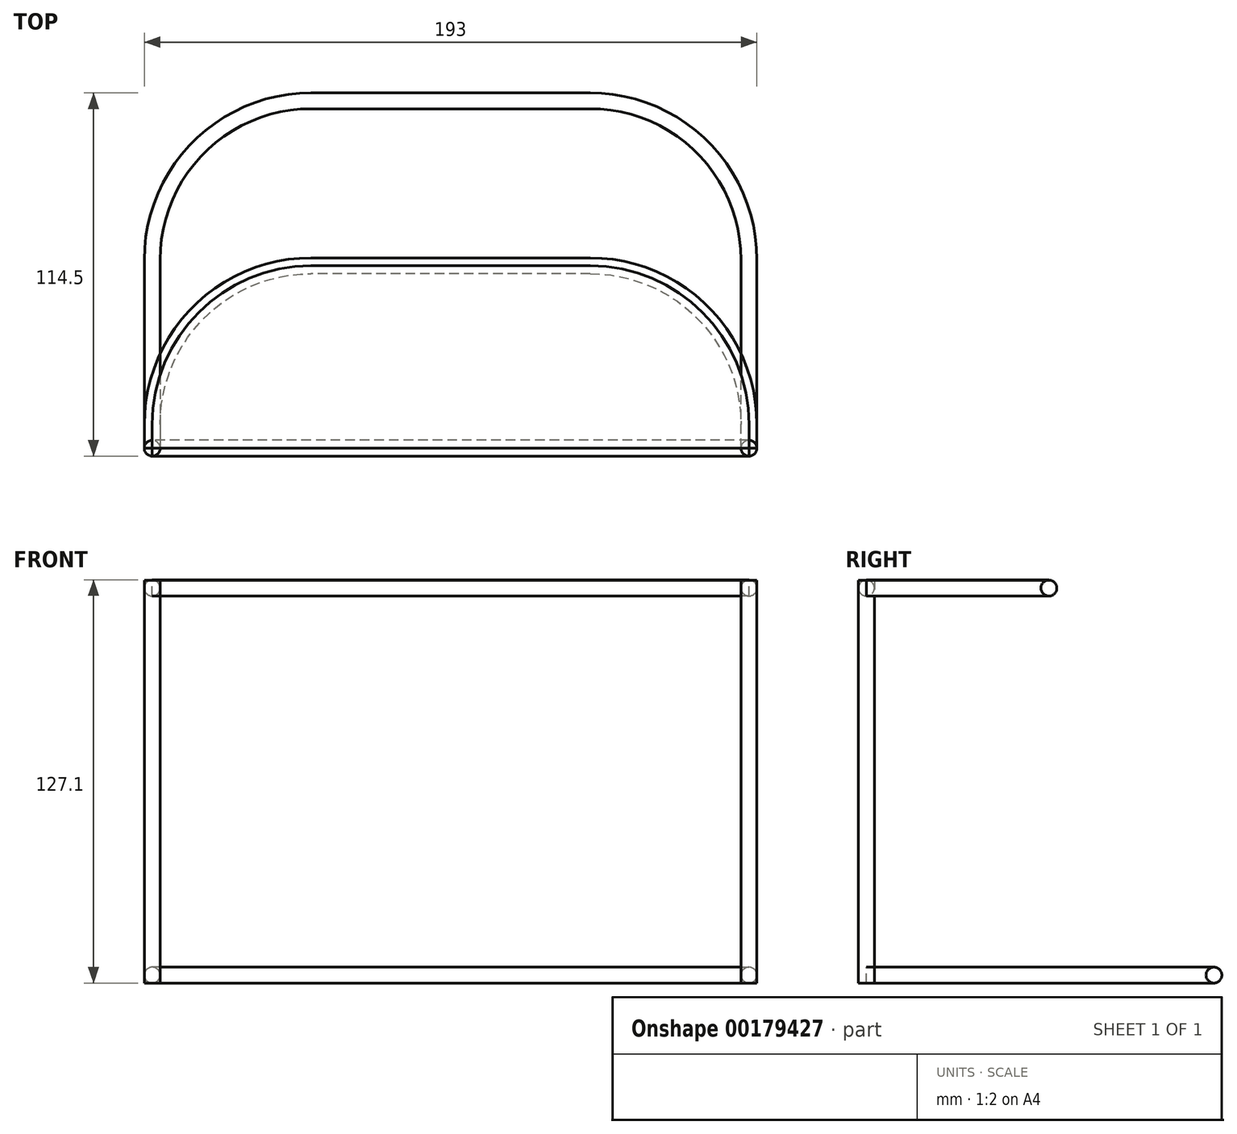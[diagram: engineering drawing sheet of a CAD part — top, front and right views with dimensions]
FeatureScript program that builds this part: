
annotation { "Feature Type Name" : "Feature", "Feature Type Description" : "" }
export const myFeature = defineFeature(function(context is Context, id is Id, definition is map)
    precondition{}
    {
        {
            var Q0;
            Q0=qCreatedBy(makeId("Top.planeOp"),FACE);
            var sketch = newSketch(context, id + "F0", { "sketchPlane" : qUnion([Q0])});
            skLineSegment(sketch, "E0", {"start": v(-94, 0) * mm, "end": v(94, 0) * mm, "construction": true});
            skCircle(sketch, "E1", {"center": v(-94, 0) * mm, "radius": 2.5 * mm});
            skCircle(sketch, "E2", {"center": v(94, 0) * mm, "radius": 2.5 * mm});
            skSolve(sketch);
        }
        {
            var Q0;
            Q0=makeQuery(id+"F0.imprint","IMPRINT",FACE,{"disambiguationData":[TD([[makeQuery(id+"F0.imprint","IMPRINT",EDGE,{"derivedFrom":sQuery(id+"F0.wireOp",EDGE,"E2")}),1.0]])]});
            var Q1;
            Q1=makeQuery(id+"F0.imprint","IMPRINT",FACE,{"disambiguationData":[TD([[makeQuery(id+"F0.imprint","IMPRINT",EDGE,{"derivedFrom":sQuery(id+"F0.wireOp",EDGE,"E1")}),1.0]])]});
            extrude(context, id + "F1", {"entities" : qUnion([Q0, Q1]), "depth" : 127 * mm});
        }
        {
            var Q0;
            Q0=qCreatedBy(makeId("Top.planeOp"),FACE);
            cPlane(context, id + "F2", {"entities" : qUnion([Q0]), "cplaneType" : CPlaneType.OFFSET, "offset" : 124.5 * mm, "width" : 150 * mm, "height" : 150 * mm});
        }
        {
            var Q0;
            Q0=qCreatedBy(id+"F2.planeOp",FACE);
            var sketch = newSketch(context, id + "F3", { "sketchPlane" : qUnion([Q0])});
            skCircle(sketch, "E3.0", {"center": v(-94, 0) * mm, "radius": 2.5 * mm});
            skCircle(sketch, "E4.0", {"center": v(94, 0) * mm, "radius": 2.5 * mm});
            skLineSegment(sketch, "E5", {"start": v(-94, 0) * mm, "end": v(94, 0) * mm});
            skSolve(sketch);
        }
        {
            var Q0;
            Q0=qCreatedBy(makeId("Right.planeOp"),FACE);
            cPlane(context, id + "F4", {"entities" : qUnion([Q0]), "cplaneType" : CPlaneType.OFFSET, "offset" : (188 / 2) * mm, "width" : 150 * mm, "height" : 150 * mm});
        }
        {
            var Q0;
            Q0=qCreatedBy(id+"F4.planeOp",FACE);
            var sketch = newSketch(context, id + "F5", { "sketchPlane" : qUnion([Q0])});
            skPoint(sketch, "E6.0", {"position": v(0, 124.5) * mm});
            skCircle(sketch, "E7", {"center": v(0, 124.5) * mm, "radius": 2.5 * mm});
            skSolve(sketch);
        }
        {
            var Q0;
            Q0=makeQuery(id+"F5.imprint","IMPRINT",FACE,{"disambiguationData":[TD([[makeQuery(id+"F5.imprint","IMPRINT",EDGE,{"derivedFrom":sQuery(id+"F5.wireOp",EDGE,"E7")}),1.0]])]});
            var Q1;
            Q1=sQuery(id+"F5.wireOp",EDGE,"E7");
            var Q2;
            Q2=sQuery(id+"F3.wireOp",EDGE,"E5");
            var Q3;
            Q3=sQuery(id+"F3.wireOp",EDGE,"E5");
            sweep(context, id + "F6", {"profiles" : qUnion([Q0]), "surfaceProfiles" : qUnion([Q1, Q2]), "path" : qUnion([Q3])});
        }
        {
            var Q0;
            Q0=qCreatedBy(makeId("Front.planeOp"),FACE);
            var sketch = newSketch(context, id + "F7", { "sketchPlane" : qUnion([Q0])});
            skCircle(sketch, "E8", {"center": v(94, 2.5) * mm, "radius": 2.5 * mm});
            skSolve(sketch);
        }
        {
            var Q0;
            Q0=qCreatedBy(makeId("Top.planeOp"),FACE);
            var sketch = newSketch(context, id + "F8", { "sketchPlane" : qUnion([Q0])});
            skLineSegment(sketch, "E9", {"start": v(94, 0) * mm, "end": v(94, 59.5) * mm});
            skLineSegment(sketch, "E10", {"start": v(44, 109.5) * mm, "end": v(-44, 109.5) * mm});
            skLineSegment(sketch, "E11", {"start": v(-94, 59.5) * mm, "end": v(-94, 0) * mm});
            skPoint(sketch, "E12.visualSharp", {"position": v(-94, 109.5) * mm});
            skArc(sketch, "E12.filletArc", {"start": v(-44, 109.5) * mm, "mid": v(-79.36, 94.86) * mm, "end": v(-94, 59.5) * mm});
            skPoint(sketch, "E13.visualSharp", {"position": v(94, 109.5) * mm});
            skArc(sketch, "E13.filletArc", {"start": v(94, 59.5) * mm, "mid": v(79.36, 94.86) * mm, "end": v(44, 109.5) * mm});
            skSolve(sketch);
        }
        {
            var Q0;
            Q0=makeQuery(id+"F7.imprint","IMPRINT",FACE,{"disambiguationData":[TD([[makeQuery(id+"F7.imprint","IMPRINT",EDGE,{"derivedFrom":sQuery(id+"F7.wireOp",EDGE,"E8")}),1.0]])]});
            var Q1;
            Q1=sQuery(id+"F8.wireOp",EDGE,"E9");
            var Q2;
            Q2=sQuery(id+"F8.wireOp",EDGE,"E13.filletArc");
            var Q3;
            Q3=sQuery(id+"F8.wireOp",EDGE,"E10");
            var Q4;
            Q4=sQuery(id+"F8.wireOp",EDGE,"E12.filletArc");
            var Q5;
            Q5=sQuery(id+"F8.wireOp",EDGE,"E11");
            sweep(context, id + "F9", {"profiles" : qUnion([Q0]), "path" : qUnion([Q1, Q2, Q3, Q4, Q5])});
        }
        {
            var Q0;
            Q0=qCreatedBy(id+"F2.planeOp",FACE);
            var sketch = newSketch(context, id + "F10", { "sketchPlane" : qUnion([Q0])});
            skLineSegment(sketch, "E14", {"start": v(94, 0) * mm, "end": v(94, 7.5) * mm});
            skLineSegment(sketch, "E15", {"start": v(44, 57.5) * mm, "end": v(-44, 57.5) * mm});
            skLineSegment(sketch, "E16", {"start": v(-94, 7.5) * mm, "end": v(-94, 0) * mm});
            skPoint(sketch, "E17.visualSharp", {"position": v(-94, 57.5) * mm});
            skArc(sketch, "E17.filletArc", {"start": v(-44, 57.5) * mm, "mid": v(-79.36, 42.86) * mm, "end": v(-94, 7.5) * mm});
            skPoint(sketch, "E18.visualSharp", {"position": v(94, 57.5) * mm});
            skArc(sketch, "E18.filletArc", {"start": v(94, 7.5) * mm, "mid": v(79.36, 42.86) * mm, "end": v(44, 57.5) * mm});
            skSolve(sketch);
        }
        {
            var Q0;
            Q0=qCreatedBy(makeId("Front.planeOp"),FACE);
            var sketch = newSketch(context, id + "F11", { "sketchPlane" : qUnion([Q0])});
            skPoint(sketch, "E19.0", {"position": v(94, 124.5) * mm});
            skCircle(sketch, "E20", {"center": v(94, 124.5) * mm, "radius": 2.5 * mm});
            skSolve(sketch);
        }
        {
            var Q0;
            Q0=makeQuery(id+"F11.imprint","IMPRINT",FACE,{"disambiguationData":[TD([[makeQuery(id+"F11.imprint","IMPRINT",EDGE,{"derivedFrom":sQuery(id+"F11.wireOp",EDGE,"E20")}),1.0]])]});
            var Q1;
            Q1=sQuery(id+"F10.wireOp",EDGE,"E14");
            var Q2;
            Q2=sQuery(id+"F10.wireOp",EDGE,"E18.filletArc");
            var Q3;
            Q3=sQuery(id+"F10.wireOp",EDGE,"E15");
            var Q4;
            Q4=sQuery(id+"F10.wireOp",EDGE,"E17.filletArc");
            var Q5;
            Q5=sQuery(id+"F10.wireOp",EDGE,"E16");
            sweep(context, id + "F12", {"profiles" : qUnion([Q0]), "path" : qUnion([Q1, Q2, Q3, Q4, Q5])});
        }
        {
            var Q0;
            Q0=qCreatedBy(id+"F2.planeOp",FACE);
            var sketch = newSketch(context, id + "F13", { "sketchPlane" : qUnion([Q0])});
            skArc(sketch, "E21", {"start": v(-44, 60) * mm, "mid": v(-81.12, 44.62) * mm, "end": v(-96.5, 7.5) * mm});
            skLineSegment(sketch, "E22", {"start": v(-96.5, 0) * mm, "end": v(-96.5, 7.5) * mm});
            skLineSegment(sketch, "E23", {"start": v(-44, 60) * mm, "end": v(44, 60) * mm});
            skArc(sketch, "E24", {"start": v(96.5, 7.5) * mm, "mid": v(81.12, 44.62) * mm, "end": v(44, 60) * mm});
            skLineSegment(sketch, "E25", {"start": v(96.5, 7.5) * mm, "end": v(96.5, 0) * mm});
            skSolve(sketch);
        }
        {
            var Q0;
            Q0=qCreatedBy(makeId("Top.planeOp"),FACE);
            cPlane(context, id + "F14", {"entities" : qUnion([Q0]), "cplaneType" : CPlaneType.OFFSET, "offset" : 2.5 * mm, "width" : 150 * mm, "height" : 150 * mm});
        }
        {
            var Q0;
            Q0=qCreatedBy(id+"F14.planeOp",FACE);
            var sketch = newSketch(context, id + "F15", { "sketchPlane" : qUnion([Q0])});
            skArc(sketch, "E26", {"start": v(-44, 112) * mm, "mid": v(-81.12, 96.62) * mm, "end": v(-96.5, 59.5) * mm});
            skLineSegment(sketch, "E27", {"start": v(-44, 112) * mm, "end": v(44, 112) * mm});
            skArc(sketch, "E28", {"start": v(96.5, 59.5) * mm, "mid": v(81.12, 96.62) * mm, "end": v(44, 112) * mm});
            skLineSegment(sketch, "E29", {"start": v(96.5, 59.5) * mm, "end": v(96.5, 0) * mm});
            skLineSegment(sketch, "E30", {"start": v(-96.5, 0) * mm, "end": v(-96.5, 59.5) * mm});
            skSolve(sketch);
        }
        {
            var Q0;
            Q0=qCreatedBy(makeId("Right.planeOp"),FACE);
            var sketch = newSketch(context, id + "F16", { "sketchPlane" : qUnion([Q0])});
            skPoint(sketch, "E31.0", {"position": v(60, 124.5) * mm});
            skPoint(sketch, "E32.0", {"position": v(112, 2.5) * mm});
            skFitSpline(sketch, "E33", {"points": [v(60, 124.5) * mm, v(112, 2.5) * mm], "startDerivative": vector(40.52, -242.4) * mm, "endDerivative": vector(1.83, -10.83) * mm});
            skSolve(sketch);
        }
        {
            var Q0;
            Q0 = qSketchRegion(id + "F13", true);
            var Q1;
            Q1 = qSketchRegion(id + "F15", true);
            var Q2;
            Q2 = qConstructionFilter(qBodyType(qCreatedBy(id + "F13" ,EDGE), BodyType.WIRE), ConstructionObject.NO);
            var Q3;
            Q3 = qConstructionFilter(qBodyType(qCreatedBy(id + "F15" ,EDGE), BodyType.WIRE), ConstructionObject.NO);
            var Q4;
            Q4 = qConstructionFilter(qBodyType(qCreatedBy(id + "F16" ,EDGE), BodyType.WIRE), ConstructionObject.NO);
            loft(context, id + "F17", {"bodyType" : ToolBodyType.SURFACE, "addGuides" : true, "sheetProfilesArray" : [{ "sheetProfileEntities" : qUnion([Q0]) }, { "sheetProfileEntities" : qUnion([Q1]) }], "wireProfilesArray" : [{ "wireProfileEntities" : qUnion([Q2]) }, { "wireProfileEntities" : qUnion([Q3]) }], "guidesArray" : [{ "guideEntities" : qUnion([Q4]), "guideDerivativeType" : LoftGuideDerivativeType.DEFAULT, "guideDerivativeMagnitude" : 1 }]});
        }
        {
            var Q0;
            Q0=qCreatedBy(id+"F2.planeOp",FACE);
            cPlane(context, id + "F18", {"entities" : qUnion([Q0]), "cplaneType" : CPlaneType.OFFSET, "offset" : 2.5 * mm, "width" : 150 * mm, "height" : 150 * mm});
        }
        {
            var Q0;
            Q0=qCreatedBy(id+"F18.planeOp",FACE);
            var sketch = newSketch(context, id + "F19", { "sketchPlane" : qUnion([Q0])});
            skLineSegment(sketch, "E34.0", {"start": v(-94, 0) * mm, "end": v(94, 0) * mm});
            skPoint(sketch, "E35.0", {"position": v(94, 0) * mm});
            skLineSegment(sketch, "E36.0", {"start": v(94, 0) * mm, "end": v(94, 7.5) * mm});
            skLineSegment(sketch, "E37.0", {"start": v(-94, 7.5) * mm, "end": v(-94, 0) * mm});
            skLineSegment(sketch, "E38", {"start": v(44, 57.5) * mm, "end": v(-44, 57.5) * mm});
            skArc(sketch, "E39", {"start": v(-44, 57.5) * mm, "mid": v(-79.36, 42.86) * mm, "end": v(-94, 7.5) * mm});
            skArc(sketch, "E40", {"start": v(94, 7.5) * mm, "mid": v(79.36, 42.86) * mm, "end": v(44, 57.5) * mm});
            skPoint(sketch, "E41.orphan", {"position": v(-94, 59.5) * mm});
            skPoint(sketch, "E42.orphan", {"position": v(94, 59.5) * mm});
            skSolve(sketch);
        }
        {
            var Q0;
            Q0 = qSketchRegion(id + "F19", true);
            var Q1;
            Q1 = qConstructionFilter(qBodyType(qCreatedBy(id + "F19" ,EDGE), BodyType.WIRE), ConstructionObject.NO);
            extrude(context, id + "F20", {"entities" : qUnion([Q0]), "surfaceEntities" : qUnion([Q1]), "depth" : 0.1 * mm});
        }
    });
